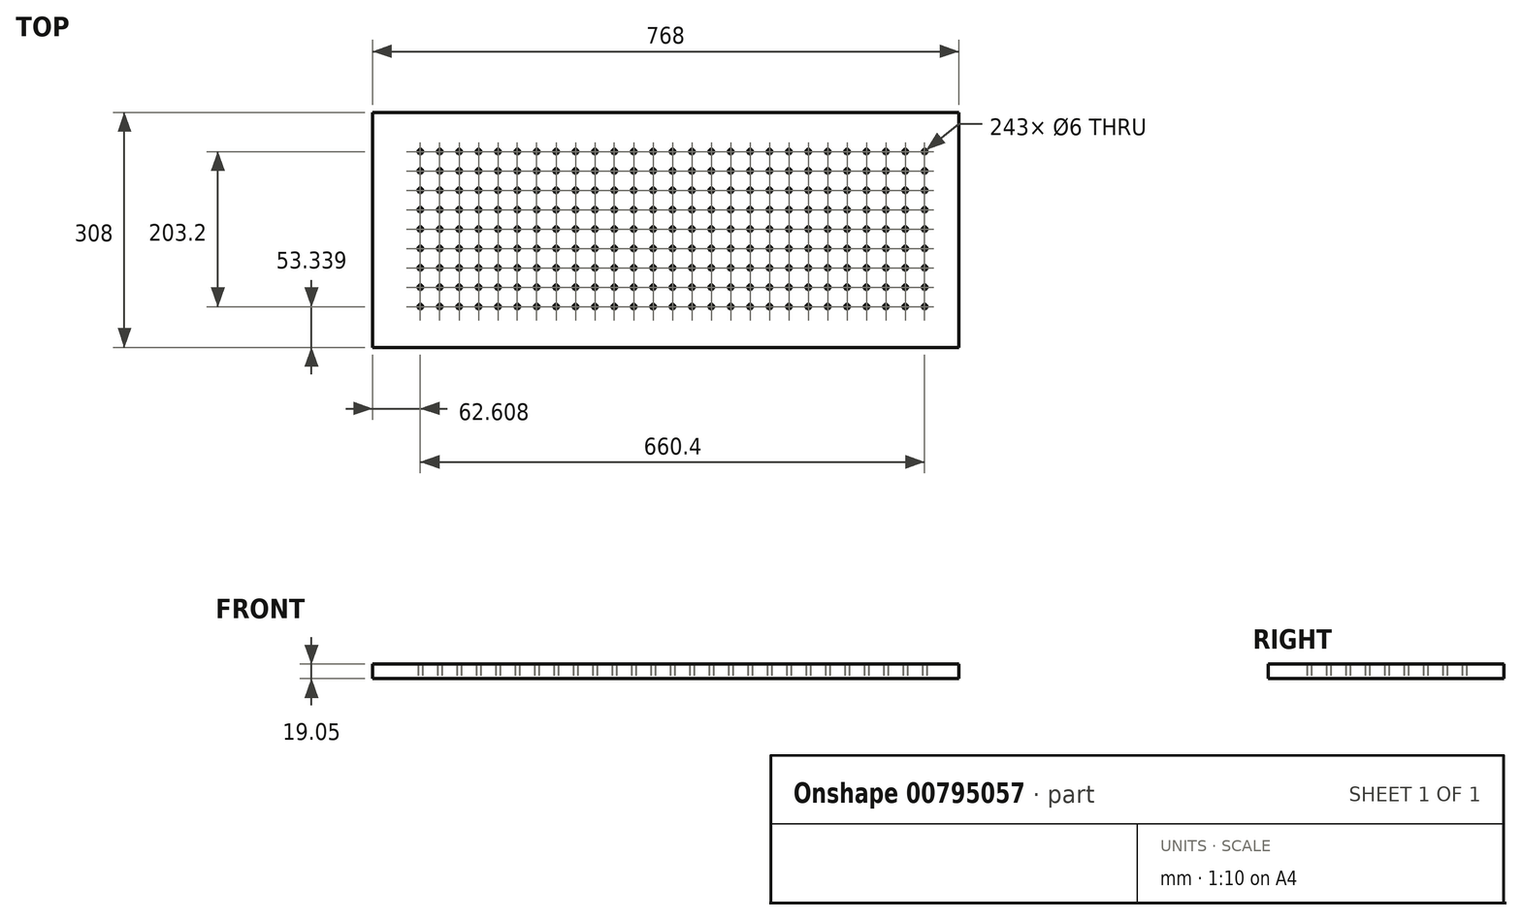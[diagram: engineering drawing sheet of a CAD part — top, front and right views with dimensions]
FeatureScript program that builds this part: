
annotation { "Feature Type Name" : "Feature", "Feature Type Description" : "" }
export const myFeature = defineFeature(function(context is Context, id is Id, definition is map)
    precondition{}
    {
        {
            var Q0;
            Q0=qCreatedBy(makeId("Top.planeOp"),FACE);
            var sketch = newSketch(context, id + "F0", { "sketchPlane" : qUnion([Q0])});
            skLineSegment(sketch, "E0", {"start": v(-588.45, -721.98) * mm, "end": v(179.55, -721.98) * mm});
            skLineSegment(sketch, "E1", {"start": v(179.55, -721.98) * mm, "end": v(179.55, -413.98) * mm});
            skLineSegment(sketch, "E2", {"start": v(179.55, -413.98) * mm, "end": v(-588.45, -413.98) * mm});
            skCircle(sketch, "E3.0.15.2", {"center": v(-475.04, -465.44) * mm, "radius": 3 * mm});
            skCircle(sketch, "E3.0.15.4", {"center": v(-297.24, -465.44) * mm, "radius": 3 * mm});
            skCircle(sketch, "E3.0.15.5", {"center": v(-246.44, -465.44) * mm, "radius": 3 * mm});
            skCircle(sketch, "E3.0.15.6", {"center": v(-373.44, -465.44) * mm, "radius": 3 * mm});
            skCircle(sketch, "E3.0.15.7", {"center": v(-94.04, -465.44) * mm, "radius": 3 * mm});
            skCircle(sketch, "E3.0.15.8", {"center": v(-348.04, -465.44) * mm, "radius": 3 * mm});
            skCircle(sketch, "E3.0.15.9", {"center": v(-144.84, -465.44) * mm, "radius": 3 * mm});
            skCircle(sketch, "E3.0.15.11", {"center": v(-424.24, -465.44) * mm, "radius": 3 * mm});
            skCircle(sketch, "E3.0.15.12", {"center": v(7.56, -465.44) * mm, "radius": 3 * mm});
            skCircle(sketch, "E3.0.15.15", {"center": v(134.56, -465.44) * mm, "radius": 3 * mm});
            skCircle(sketch, "E3.0.15.17", {"center": v(109.16, -465.44) * mm, "radius": 3 * mm});
            skCircle(sketch, "E3.0.15.18", {"center": v(-119.44, -465.44) * mm, "radius": 3 * mm});
            skCircle(sketch, "E3.0.15.20", {"center": v(83.76, -465.44) * mm, "radius": 3 * mm});
            skCircle(sketch, "E3.0.15.21", {"center": v(-500.44, -465.44) * mm, "radius": 3 * mm});
            skCircle(sketch, "E3.0.15.22", {"center": v(58.36, -465.44) * mm, "radius": 3 * mm});
            skCircle(sketch, "E3.0.15.23", {"center": v(-525.84, -465.44) * mm, "radius": 3 * mm});
            skCircle(sketch, "E3.0.15.24", {"center": v(-17.84, -465.44) * mm, "radius": 3 * mm});
            skCircle(sketch, "E3.0.15.25", {"center": v(-398.84, -465.44) * mm, "radius": 3 * mm});
            skCircle(sketch, "E3.0.15.27", {"center": v(-43.24, -465.44) * mm, "radius": 3 * mm});
            skCircle(sketch, "E3.0.15.28", {"center": v(-68.64, -465.44) * mm, "radius": 3 * mm});
            skCircle(sketch, "E3.0.15.29", {"center": v(-322.64, -465.44) * mm, "radius": 3 * mm});
            skCircle(sketch, "E3.0.15.30", {"center": v(-221.04, -465.44) * mm, "radius": 3 * mm});
            skCircle(sketch, "E3.0.15.31", {"center": v(-195.64, -465.44) * mm, "radius": 3 * mm});
            skCircle(sketch, "E3.0.15.32", {"center": v(-170.24, -465.44) * mm, "radius": 3 * mm});
            skCircle(sketch, "E3.0.15.34", {"center": v(-449.64, -465.44) * mm, "radius": 3 * mm});
            skCircle(sketch, "E3.0.15.35", {"center": v(-271.84, -465.44) * mm, "radius": 3 * mm});
            skCircle(sketch, "E3.0.15.36", {"center": v(32.96, -465.44) * mm, "radius": 3 * mm});
            skCircle(sketch, "E3.0.15.37", {"center": v(-500.44, -465.44) * mm, "radius": 3 * mm});
            skCircle(sketch, "E3.0.15.38", {"center": v(-43.24, -465.44) * mm, "radius": 3 * mm});
            skCircle(sketch, "E3.0.15.39", {"center": v(-348.04, -465.44) * mm, "radius": 3 * mm});
            skCircle(sketch, "E3.0.15.40", {"center": v(-68.64, -465.44) * mm, "radius": 3 * mm});
            skCircle(sketch, "E3.0.15.41", {"center": v(-398.84, -465.44) * mm, "radius": 3 * mm});
            skCircle(sketch, "E3.0.15.42", {"center": v(-246.44, -465.44) * mm, "radius": 3 * mm});
            skCircle(sketch, "E3.0.15.44", {"center": v(32.96, -465.44) * mm, "radius": 3 * mm});
            skCircle(sketch, "E3.0.15.45", {"center": v(-195.64, -465.44) * mm, "radius": 3 * mm});
            skCircle(sketch, "E3.0.15.47", {"center": v(-322.64, -465.44) * mm, "radius": 3 * mm});
            skCircle(sketch, "E3.0.15.49", {"center": v(-17.84, -465.44) * mm, "radius": 3 * mm});
            skCircle(sketch, "E3.0.15.50", {"center": v(134.56, -465.44) * mm, "radius": 3 * mm});
            skCircle(sketch, "E3.0.15.51", {"center": v(-449.64, -465.44) * mm, "radius": 3 * mm});
            skCircle(sketch, "E3.0.15.53", {"center": v(-170.24, -465.44) * mm, "radius": 3 * mm});
            skCircle(sketch, "E3.0.15.54", {"center": v(-119.44, -465.44) * mm, "radius": 3 * mm});
            skCircle(sketch, "E3.0.15.55", {"center": v(-373.44, -465.44) * mm, "radius": 3 * mm});
            skCircle(sketch, "E3.0.15.56", {"center": v(109.16, -465.44) * mm, "radius": 3 * mm});
            skCircle(sketch, "E3.0.15.57", {"center": v(-424.24, -465.44) * mm, "radius": 3 * mm});
            skCircle(sketch, "E3.0.15.58", {"center": v(-525.84, -465.44) * mm, "radius": 3 * mm});
            skCircle(sketch, "E3.0.15.59", {"center": v(-94.04, -465.44) * mm, "radius": 3 * mm});
            skCircle(sketch, "E3.0.15.60", {"center": v(-475.04, -465.44) * mm, "radius": 3 * mm});
            skCircle(sketch, "E3.0.15.61", {"center": v(58.36, -465.44) * mm, "radius": 3 * mm});
            skCircle(sketch, "E3.0.15.63", {"center": v(7.56, -465.44) * mm, "radius": 3 * mm});
            skCircle(sketch, "E3.0.15.64", {"center": v(-297.24, -465.44) * mm, "radius": 3 * mm});
            skCircle(sketch, "E3.0.15.67", {"center": v(-144.84, -465.44) * mm, "radius": 3 * mm});
            skCircle(sketch, "E3.0.15.68", {"center": v(-221.04, -465.44) * mm, "radius": 3 * mm});
            skCircle(sketch, "E3.0.15.69", {"center": v(-271.84, -465.44) * mm, "radius": 3 * mm});
            skCircle(sketch, "E3.0.15.70", {"center": v(83.76, -465.44) * mm, "radius": 3 * mm});
            skCircle(sketch, "E3.0.15.71", {"center": v(134.56, -465.44) * mm, "radius": 3 * mm});
            skCircle(sketch, "E3.0.15.72", {"center": v(-424.24, -465.44) * mm, "radius": 3 * mm});
            skCircle(sketch, "E3.0.15.73", {"center": v(-195.64, -465.44) * mm, "radius": 3 * mm});
            skCircle(sketch, "E3.0.15.74", {"center": v(-525.84, -465.44) * mm, "radius": 3 * mm});
            skCircle(sketch, "E3.0.15.75", {"center": v(109.16, -465.44) * mm, "radius": 3 * mm});
            skCircle(sketch, "E3.0.15.76", {"center": v(-246.44, -465.44) * mm, "radius": 3 * mm});
            skCircle(sketch, "E3.0.15.77", {"center": v(-449.64, -465.44) * mm, "radius": 3 * mm});
            skCircle(sketch, "E3.0.15.78", {"center": v(-144.84, -465.44) * mm, "radius": 3 * mm});
            skCircle(sketch, "E3.0.15.79", {"center": v(-348.04, -465.44) * mm, "radius": 3 * mm});
            skCircle(sketch, "E3.0.15.80", {"center": v(-94.04, -465.44) * mm, "radius": 3 * mm});
            skCircle(sketch, "E3.0.15.81", {"center": v(32.96, -465.44) * mm, "radius": 3 * mm});
            skCircle(sketch, "E3.0.15.82", {"center": v(-68.64, -465.44) * mm, "radius": 3 * mm});
            skCircle(sketch, "E3.0.15.84", {"center": v(-373.44, -465.44) * mm, "radius": 3 * mm});
            skCircle(sketch, "E3.0.15.86", {"center": v(-170.24, -465.44) * mm, "radius": 3 * mm});
            skCircle(sketch, "E3.0.15.88", {"center": v(-17.84, -465.44) * mm, "radius": 3 * mm});
            skCircle(sketch, "E3.0.15.89", {"center": v(-221.04, -465.44) * mm, "radius": 3 * mm});
            skCircle(sketch, "E3.0.15.90", {"center": v(-119.44, -465.44) * mm, "radius": 3 * mm});
            skCircle(sketch, "E3.0.15.92", {"center": v(-475.04, -465.44) * mm, "radius": 3 * mm});
            skCircle(sketch, "E3.0.15.93", {"center": v(-297.24, -465.44) * mm, "radius": 3 * mm});
            skCircle(sketch, "E3.0.15.94", {"center": v(-43.24, -465.44) * mm, "radius": 3 * mm});
            skCircle(sketch, "E3.0.15.95", {"center": v(83.76, -465.44) * mm, "radius": 3 * mm});
            skCircle(sketch, "E3.0.15.97", {"center": v(-500.44, -465.44) * mm, "radius": 3 * mm});
            skCircle(sketch, "E3.0.15.98", {"center": v(-322.64, -465.44) * mm, "radius": 3 * mm});
            skCircle(sketch, "E3.0.15.100", {"center": v(-398.84, -465.44) * mm, "radius": 3 * mm});
            skCircle(sketch, "E3.0.15.102", {"center": v(58.36, -465.44) * mm, "radius": 3 * mm});
            skCircle(sketch, "E3.0.15.103", {"center": v(7.56, -465.44) * mm, "radius": 3 * mm});
            skCircle(sketch, "E3.0.15.104", {"center": v(-271.84, -465.44) * mm, "radius": 3 * mm});
            skCircle(sketch, "E3.0.16.2", {"center": v(-475.04, -490.84) * mm, "radius": 3 * mm});
            skCircle(sketch, "E3.0.16.4", {"center": v(-297.24, -490.84) * mm, "radius": 3 * mm});
            skCircle(sketch, "E3.0.16.5", {"center": v(-246.44, -490.84) * mm, "radius": 3 * mm});
            skCircle(sketch, "E3.0.16.6", {"center": v(-373.44, -490.84) * mm, "radius": 3 * mm});
            skCircle(sketch, "E3.0.16.7", {"center": v(-94.04, -490.84) * mm, "radius": 3 * mm});
            skCircle(sketch, "E3.0.16.8", {"center": v(-348.04, -490.84) * mm, "radius": 3 * mm});
            skCircle(sketch, "E3.0.16.9", {"center": v(-144.84, -490.84) * mm, "radius": 3 * mm});
            skCircle(sketch, "E3.0.16.11", {"center": v(-424.24, -490.84) * mm, "radius": 3 * mm});
            skCircle(sketch, "E3.0.16.12", {"center": v(7.56, -490.84) * mm, "radius": 3 * mm});
            skCircle(sketch, "E3.0.16.15", {"center": v(134.56, -490.84) * mm, "radius": 3 * mm});
            skCircle(sketch, "E3.0.16.17", {"center": v(109.16, -490.84) * mm, "radius": 3 * mm});
            skCircle(sketch, "E3.0.16.18", {"center": v(-119.44, -490.84) * mm, "radius": 3 * mm});
            skCircle(sketch, "E3.0.16.20", {"center": v(83.76, -490.84) * mm, "radius": 3 * mm});
            skCircle(sketch, "E3.0.16.21", {"center": v(-500.44, -490.84) * mm, "radius": 3 * mm});
            skCircle(sketch, "E3.0.16.22", {"center": v(58.36, -490.84) * mm, "radius": 3 * mm});
            skCircle(sketch, "E3.0.16.23", {"center": v(-525.84, -490.84) * mm, "radius": 3 * mm});
            skCircle(sketch, "E3.0.16.24", {"center": v(-17.84, -490.84) * mm, "radius": 3 * mm});
            skCircle(sketch, "E3.0.16.25", {"center": v(-398.84, -490.84) * mm, "radius": 3 * mm});
            skCircle(sketch, "E3.0.16.27", {"center": v(-43.24, -490.84) * mm, "radius": 3 * mm});
            skCircle(sketch, "E3.0.16.28", {"center": v(-68.64, -490.84) * mm, "radius": 3 * mm});
            skCircle(sketch, "E3.0.16.29", {"center": v(-322.64, -490.84) * mm, "radius": 3 * mm});
            skCircle(sketch, "E3.0.16.30", {"center": v(-221.04, -490.84) * mm, "radius": 3 * mm});
            skCircle(sketch, "E3.0.16.31", {"center": v(-195.64, -490.84) * mm, "radius": 3 * mm});
            skCircle(sketch, "E3.0.16.32", {"center": v(-170.24, -490.84) * mm, "radius": 3 * mm});
            skCircle(sketch, "E3.0.16.34", {"center": v(-449.64, -490.84) * mm, "radius": 3 * mm});
            skCircle(sketch, "E3.0.16.35", {"center": v(-271.84, -490.84) * mm, "radius": 3 * mm});
            skCircle(sketch, "E3.0.16.36", {"center": v(32.96, -490.84) * mm, "radius": 3 * mm});
            skCircle(sketch, "E3.0.16.37", {"center": v(-500.44, -490.84) * mm, "radius": 3 * mm});
            skCircle(sketch, "E3.0.16.38", {"center": v(-43.24, -490.84) * mm, "radius": 3 * mm});
            skCircle(sketch, "E3.0.16.39", {"center": v(-348.04, -490.84) * mm, "radius": 3 * mm});
            skCircle(sketch, "E3.0.16.40", {"center": v(-68.64, -490.84) * mm, "radius": 3 * mm});
            skCircle(sketch, "E3.0.16.41", {"center": v(-398.84, -490.84) * mm, "radius": 3 * mm});
            skCircle(sketch, "E3.0.16.42", {"center": v(-246.44, -490.84) * mm, "radius": 3 * mm});
            skCircle(sketch, "E3.0.16.44", {"center": v(32.96, -490.84) * mm, "radius": 3 * mm});
            skCircle(sketch, "E3.0.16.45", {"center": v(-195.64, -490.84) * mm, "radius": 3 * mm});
            skCircle(sketch, "E3.0.16.47", {"center": v(-322.64, -490.84) * mm, "radius": 3 * mm});
            skCircle(sketch, "E3.0.16.49", {"center": v(-17.84, -490.84) * mm, "radius": 3 * mm});
            skCircle(sketch, "E3.0.16.50", {"center": v(134.56, -490.84) * mm, "radius": 3 * mm});
            skCircle(sketch, "E3.0.16.51", {"center": v(-449.64, -490.84) * mm, "radius": 3 * mm});
            skCircle(sketch, "E3.0.16.53", {"center": v(-170.24, -490.84) * mm, "radius": 3 * mm});
            skCircle(sketch, "E3.0.16.54", {"center": v(-119.44, -490.84) * mm, "radius": 3 * mm});
            skCircle(sketch, "E3.0.16.55", {"center": v(-373.44, -490.84) * mm, "radius": 3 * mm});
            skCircle(sketch, "E3.0.16.56", {"center": v(109.16, -490.84) * mm, "radius": 3 * mm});
            skCircle(sketch, "E3.0.16.57", {"center": v(-424.24, -490.84) * mm, "radius": 3 * mm});
            skCircle(sketch, "E3.0.16.58", {"center": v(-525.84, -490.84) * mm, "radius": 3 * mm});
            skCircle(sketch, "E3.0.16.59", {"center": v(-94.04, -490.84) * mm, "radius": 3 * mm});
            skCircle(sketch, "E3.0.16.60", {"center": v(-475.04, -490.84) * mm, "radius": 3 * mm});
            skCircle(sketch, "E3.0.16.61", {"center": v(58.36, -490.84) * mm, "radius": 3 * mm});
            skCircle(sketch, "E3.0.16.63", {"center": v(7.56, -490.84) * mm, "radius": 3 * mm});
            skCircle(sketch, "E3.0.16.64", {"center": v(-297.24, -490.84) * mm, "radius": 3 * mm});
            skCircle(sketch, "E3.0.16.67", {"center": v(-144.84, -490.84) * mm, "radius": 3 * mm});
            skCircle(sketch, "E3.0.16.68", {"center": v(-221.04, -490.84) * mm, "radius": 3 * mm});
            skCircle(sketch, "E3.0.16.69", {"center": v(-271.84, -490.84) * mm, "radius": 3 * mm});
            skCircle(sketch, "E3.0.16.70", {"center": v(83.76, -490.84) * mm, "radius": 3 * mm});
            skCircle(sketch, "E3.0.16.71", {"center": v(134.56, -490.84) * mm, "radius": 3 * mm});
            skCircle(sketch, "E3.0.16.72", {"center": v(-424.24, -490.84) * mm, "radius": 3 * mm});
            skCircle(sketch, "E3.0.16.73", {"center": v(-195.64, -490.84) * mm, "radius": 3 * mm});
            skCircle(sketch, "E3.0.16.74", {"center": v(-525.84, -490.84) * mm, "radius": 3 * mm});
            skCircle(sketch, "E3.0.16.75", {"center": v(109.16, -490.84) * mm, "radius": 3 * mm});
            skCircle(sketch, "E3.0.16.76", {"center": v(-246.44, -490.84) * mm, "radius": 3 * mm});
            skCircle(sketch, "E3.0.16.77", {"center": v(-449.64, -490.84) * mm, "radius": 3 * mm});
            skCircle(sketch, "E3.0.16.78", {"center": v(-144.84, -490.84) * mm, "radius": 3 * mm});
            skCircle(sketch, "E3.0.16.79", {"center": v(-348.04, -490.84) * mm, "radius": 3 * mm});
            skCircle(sketch, "E3.0.16.80", {"center": v(-94.04, -490.84) * mm, "radius": 3 * mm});
            skCircle(sketch, "E3.0.16.81", {"center": v(32.96, -490.84) * mm, "radius": 3 * mm});
            skCircle(sketch, "E3.0.16.82", {"center": v(-68.64, -490.84) * mm, "radius": 3 * mm});
            skCircle(sketch, "E3.0.16.84", {"center": v(-373.44, -490.84) * mm, "radius": 3 * mm});
            skCircle(sketch, "E3.0.16.86", {"center": v(-170.24, -490.84) * mm, "radius": 3 * mm});
            skCircle(sketch, "E3.0.16.88", {"center": v(-17.84, -490.84) * mm, "radius": 3 * mm});
            skCircle(sketch, "E3.0.16.89", {"center": v(-221.04, -490.84) * mm, "radius": 3 * mm});
            skCircle(sketch, "E3.0.16.90", {"center": v(-119.44, -490.84) * mm, "radius": 3 * mm});
            skCircle(sketch, "E3.0.16.92", {"center": v(-475.04, -490.84) * mm, "radius": 3 * mm});
            skCircle(sketch, "E3.0.16.93", {"center": v(-297.24, -490.84) * mm, "radius": 3 * mm});
            skCircle(sketch, "E3.0.16.94", {"center": v(-43.24, -490.84) * mm, "radius": 3 * mm});
            skCircle(sketch, "E3.0.16.95", {"center": v(83.76, -490.84) * mm, "radius": 3 * mm});
            skCircle(sketch, "E3.0.16.97", {"center": v(-500.44, -490.84) * mm, "radius": 3 * mm});
            skCircle(sketch, "E3.0.16.98", {"center": v(-322.64, -490.84) * mm, "radius": 3 * mm});
            skCircle(sketch, "E3.0.16.100", {"center": v(-398.84, -490.84) * mm, "radius": 3 * mm});
            skCircle(sketch, "E3.0.16.102", {"center": v(58.36, -490.84) * mm, "radius": 3 * mm});
            skCircle(sketch, "E3.0.16.103", {"center": v(7.56, -490.84) * mm, "radius": 3 * mm});
            skCircle(sketch, "E3.0.16.104", {"center": v(-271.84, -490.84) * mm, "radius": 3 * mm});
            skCircle(sketch, "E3.0.17.2", {"center": v(-475.04, -516.24) * mm, "radius": 3 * mm});
            skCircle(sketch, "E3.0.17.4", {"center": v(-297.24, -516.24) * mm, "radius": 3 * mm});
            skCircle(sketch, "E3.0.17.5", {"center": v(-246.44, -516.24) * mm, "radius": 3 * mm});
            skCircle(sketch, "E3.0.17.6", {"center": v(-373.44, -516.24) * mm, "radius": 3 * mm});
            skCircle(sketch, "E3.0.17.7", {"center": v(-94.04, -516.24) * mm, "radius": 3 * mm});
            skCircle(sketch, "E3.0.17.8", {"center": v(-348.04, -516.24) * mm, "radius": 3 * mm});
            skCircle(sketch, "E3.0.17.9", {"center": v(-144.84, -516.24) * mm, "radius": 3 * mm});
            skCircle(sketch, "E3.0.17.11", {"center": v(-424.24, -516.24) * mm, "radius": 3 * mm});
            skCircle(sketch, "E3.0.17.12", {"center": v(7.56, -516.24) * mm, "radius": 3 * mm});
            skCircle(sketch, "E3.0.17.15", {"center": v(134.56, -516.24) * mm, "radius": 3 * mm});
            skCircle(sketch, "E3.0.17.17", {"center": v(109.16, -516.24) * mm, "radius": 3 * mm});
            skCircle(sketch, "E3.0.17.18", {"center": v(-119.44, -516.24) * mm, "radius": 3 * mm});
            skCircle(sketch, "E3.0.17.20", {"center": v(83.76, -516.24) * mm, "radius": 3 * mm});
            skCircle(sketch, "E3.0.17.21", {"center": v(-500.44, -516.24) * mm, "radius": 3 * mm});
            skCircle(sketch, "E3.0.17.22", {"center": v(58.36, -516.24) * mm, "radius": 3 * mm});
            skCircle(sketch, "E3.0.17.23", {"center": v(-525.84, -516.24) * mm, "radius": 3 * mm});
            skCircle(sketch, "E3.0.17.24", {"center": v(-17.84, -516.24) * mm, "radius": 3 * mm});
            skCircle(sketch, "E3.0.17.25", {"center": v(-398.84, -516.24) * mm, "radius": 3 * mm});
            skCircle(sketch, "E3.0.17.27", {"center": v(-43.24, -516.24) * mm, "radius": 3 * mm});
            skCircle(sketch, "E3.0.17.28", {"center": v(-68.64, -516.24) * mm, "radius": 3 * mm});
            skCircle(sketch, "E3.0.17.29", {"center": v(-322.64, -516.24) * mm, "radius": 3 * mm});
            skCircle(sketch, "E3.0.17.30", {"center": v(-221.04, -516.24) * mm, "radius": 3 * mm});
            skCircle(sketch, "E3.0.17.31", {"center": v(-195.64, -516.24) * mm, "radius": 3 * mm});
            skCircle(sketch, "E3.0.17.32", {"center": v(-170.24, -516.24) * mm, "radius": 3 * mm});
            skCircle(sketch, "E3.0.17.34", {"center": v(-449.64, -516.24) * mm, "radius": 3 * mm});
            skCircle(sketch, "E3.0.17.35", {"center": v(-271.84, -516.24) * mm, "radius": 3 * mm});
            skCircle(sketch, "E3.0.17.36", {"center": v(32.96, -516.24) * mm, "radius": 3 * mm});
            skCircle(sketch, "E3.0.17.37", {"center": v(-500.44, -516.24) * mm, "radius": 3 * mm});
            skCircle(sketch, "E3.0.17.38", {"center": v(-43.24, -516.24) * mm, "radius": 3 * mm});
            skCircle(sketch, "E3.0.17.39", {"center": v(-348.04, -516.24) * mm, "radius": 3 * mm});
            skCircle(sketch, "E3.0.17.40", {"center": v(-68.64, -516.24) * mm, "radius": 3 * mm});
            skCircle(sketch, "E3.0.17.41", {"center": v(-398.84, -516.24) * mm, "radius": 3 * mm});
            skCircle(sketch, "E3.0.17.42", {"center": v(-246.44, -516.24) * mm, "radius": 3 * mm});
            skCircle(sketch, "E3.0.17.44", {"center": v(32.96, -516.24) * mm, "radius": 3 * mm});
            skCircle(sketch, "E3.0.17.45", {"center": v(-195.64, -516.24) * mm, "radius": 3 * mm});
            skCircle(sketch, "E3.0.17.47", {"center": v(-322.64, -516.24) * mm, "radius": 3 * mm});
            skCircle(sketch, "E3.0.17.49", {"center": v(-17.84, -516.24) * mm, "radius": 3 * mm});
            skCircle(sketch, "E3.0.17.50", {"center": v(134.56, -516.24) * mm, "radius": 3 * mm});
            skCircle(sketch, "E3.0.17.51", {"center": v(-449.64, -516.24) * mm, "radius": 3 * mm});
            skCircle(sketch, "E3.0.17.53", {"center": v(-170.24, -516.24) * mm, "radius": 3 * mm});
            skCircle(sketch, "E3.0.17.54", {"center": v(-119.44, -516.24) * mm, "radius": 3 * mm});
            skCircle(sketch, "E3.0.17.55", {"center": v(-373.44, -516.24) * mm, "radius": 3 * mm});
            skCircle(sketch, "E3.0.17.56", {"center": v(109.16, -516.24) * mm, "radius": 3 * mm});
            skCircle(sketch, "E3.0.17.57", {"center": v(-424.24, -516.24) * mm, "radius": 3 * mm});
            skCircle(sketch, "E3.0.17.58", {"center": v(-525.84, -516.24) * mm, "radius": 3 * mm});
            skCircle(sketch, "E3.0.17.59", {"center": v(-94.04, -516.24) * mm, "radius": 3 * mm});
            skCircle(sketch, "E3.0.17.60", {"center": v(-475.04, -516.24) * mm, "radius": 3 * mm});
            skCircle(sketch, "E3.0.17.61", {"center": v(58.36, -516.24) * mm, "radius": 3 * mm});
            skCircle(sketch, "E3.0.17.63", {"center": v(7.56, -516.24) * mm, "radius": 3 * mm});
            skCircle(sketch, "E3.0.17.64", {"center": v(-297.24, -516.24) * mm, "radius": 3 * mm});
            skCircle(sketch, "E3.0.17.67", {"center": v(-144.84, -516.24) * mm, "radius": 3 * mm});
            skCircle(sketch, "E3.0.17.68", {"center": v(-221.04, -516.24) * mm, "radius": 3 * mm});
            skCircle(sketch, "E3.0.17.69", {"center": v(-271.84, -516.24) * mm, "radius": 3 * mm});
            skCircle(sketch, "E3.0.17.70", {"center": v(83.76, -516.24) * mm, "radius": 3 * mm});
            skCircle(sketch, "E3.0.17.71", {"center": v(134.56, -516.24) * mm, "radius": 3 * mm});
            skCircle(sketch, "E3.0.17.72", {"center": v(-424.24, -516.24) * mm, "radius": 3 * mm});
            skCircle(sketch, "E3.0.17.73", {"center": v(-195.64, -516.24) * mm, "radius": 3 * mm});
            skCircle(sketch, "E3.0.17.74", {"center": v(-525.84, -516.24) * mm, "radius": 3 * mm});
            skCircle(sketch, "E3.0.17.75", {"center": v(109.16, -516.24) * mm, "radius": 3 * mm});
            skCircle(sketch, "E3.0.17.76", {"center": v(-246.44, -516.24) * mm, "radius": 3 * mm});
            skCircle(sketch, "E3.0.17.77", {"center": v(-449.64, -516.24) * mm, "radius": 3 * mm});
            skCircle(sketch, "E3.0.17.78", {"center": v(-144.84, -516.24) * mm, "radius": 3 * mm});
            skCircle(sketch, "E3.0.17.79", {"center": v(-348.04, -516.24) * mm, "radius": 3 * mm});
            skCircle(sketch, "E3.0.17.80", {"center": v(-94.04, -516.24) * mm, "radius": 3 * mm});
            skCircle(sketch, "E3.0.17.81", {"center": v(32.96, -516.24) * mm, "radius": 3 * mm});
            skCircle(sketch, "E3.0.17.82", {"center": v(-68.64, -516.24) * mm, "radius": 3 * mm});
            skCircle(sketch, "E3.0.17.84", {"center": v(-373.44, -516.24) * mm, "radius": 3 * mm});
            skCircle(sketch, "E3.0.17.86", {"center": v(-170.24, -516.24) * mm, "radius": 3 * mm});
            skCircle(sketch, "E3.0.17.88", {"center": v(-17.84, -516.24) * mm, "radius": 3 * mm});
            skCircle(sketch, "E3.0.17.89", {"center": v(-221.04, -516.24) * mm, "radius": 3 * mm});
            skCircle(sketch, "E3.0.17.90", {"center": v(-119.44, -516.24) * mm, "radius": 3 * mm});
            skCircle(sketch, "E3.0.17.92", {"center": v(-475.04, -516.24) * mm, "radius": 3 * mm});
            skCircle(sketch, "E3.0.17.93", {"center": v(-297.24, -516.24) * mm, "radius": 3 * mm});
            skCircle(sketch, "E3.0.17.94", {"center": v(-43.24, -516.24) * mm, "radius": 3 * mm});
            skCircle(sketch, "E3.0.17.95", {"center": v(83.76, -516.24) * mm, "radius": 3 * mm});
            skCircle(sketch, "E3.0.17.97", {"center": v(-500.44, -516.24) * mm, "radius": 3 * mm});
            skCircle(sketch, "E3.0.17.98", {"center": v(-322.64, -516.24) * mm, "radius": 3 * mm});
            skCircle(sketch, "E3.0.17.100", {"center": v(-398.84, -516.24) * mm, "radius": 3 * mm});
            skCircle(sketch, "E3.0.17.102", {"center": v(58.36, -516.24) * mm, "radius": 3 * mm});
            skCircle(sketch, "E3.0.17.103", {"center": v(7.56, -516.24) * mm, "radius": 3 * mm});
            skCircle(sketch, "E3.0.17.104", {"center": v(-271.84, -516.24) * mm, "radius": 3 * mm});
            skCircle(sketch, "E3.0.18.2", {"center": v(-475.04, -541.64) * mm, "radius": 3 * mm});
            skCircle(sketch, "E3.0.18.4", {"center": v(-297.24, -541.64) * mm, "radius": 3 * mm});
            skCircle(sketch, "E3.0.18.5", {"center": v(-246.44, -541.64) * mm, "radius": 3 * mm});
            skCircle(sketch, "E3.0.18.6", {"center": v(-373.44, -541.64) * mm, "radius": 3 * mm});
            skCircle(sketch, "E3.0.18.7", {"center": v(-94.04, -541.64) * mm, "radius": 3 * mm});
            skCircle(sketch, "E3.0.18.8", {"center": v(-348.04, -541.64) * mm, "radius": 3 * mm});
            skCircle(sketch, "E3.0.18.9", {"center": v(-144.84, -541.64) * mm, "radius": 3 * mm});
            skCircle(sketch, "E3.0.18.11", {"center": v(-424.24, -541.64) * mm, "radius": 3 * mm});
            skCircle(sketch, "E3.0.18.12", {"center": v(7.56, -541.64) * mm, "radius": 3 * mm});
            skCircle(sketch, "E3.0.18.15", {"center": v(134.56, -541.64) * mm, "radius": 3 * mm});
            skCircle(sketch, "E3.0.18.17", {"center": v(109.16, -541.64) * mm, "radius": 3 * mm});
            skCircle(sketch, "E3.0.18.18", {"center": v(-119.44, -541.64) * mm, "radius": 3 * mm});
            skCircle(sketch, "E3.0.18.20", {"center": v(83.76, -541.64) * mm, "radius": 3 * mm});
            skCircle(sketch, "E3.0.18.21", {"center": v(-500.44, -541.64) * mm, "radius": 3 * mm});
            skCircle(sketch, "E3.0.18.22", {"center": v(58.36, -541.64) * mm, "radius": 3 * mm});
            skCircle(sketch, "E3.0.18.23", {"center": v(-525.84, -541.64) * mm, "radius": 3 * mm});
            skCircle(sketch, "E3.0.18.24", {"center": v(-17.84, -541.64) * mm, "radius": 3 * mm});
            skCircle(sketch, "E3.0.18.25", {"center": v(-398.84, -541.64) * mm, "radius": 3 * mm});
            skCircle(sketch, "E3.0.18.27", {"center": v(-43.24, -541.64) * mm, "radius": 3 * mm});
            skCircle(sketch, "E3.0.18.28", {"center": v(-68.64, -541.64) * mm, "radius": 3 * mm});
            skCircle(sketch, "E3.0.18.29", {"center": v(-322.64, -541.64) * mm, "radius": 3 * mm});
            skCircle(sketch, "E3.0.18.30", {"center": v(-221.04, -541.64) * mm, "radius": 3 * mm});
            skCircle(sketch, "E3.0.18.31", {"center": v(-195.64, -541.64) * mm, "radius": 3 * mm});
            skCircle(sketch, "E3.0.18.32", {"center": v(-170.24, -541.64) * mm, "radius": 3 * mm});
            skCircle(sketch, "E3.0.18.34", {"center": v(-449.64, -541.64) * mm, "radius": 3 * mm});
            skCircle(sketch, "E3.0.18.35", {"center": v(-271.84, -541.64) * mm, "radius": 3 * mm});
            skCircle(sketch, "E3.0.18.36", {"center": v(32.96, -541.64) * mm, "radius": 3 * mm});
            skCircle(sketch, "E3.0.18.37", {"center": v(-500.44, -541.64) * mm, "radius": 3 * mm});
            skCircle(sketch, "E3.0.18.38", {"center": v(-43.24, -541.64) * mm, "radius": 3 * mm});
            skCircle(sketch, "E3.0.18.39", {"center": v(-348.04, -541.64) * mm, "radius": 3 * mm});
            skCircle(sketch, "E3.0.18.40", {"center": v(-68.64, -541.64) * mm, "radius": 3 * mm});
            skCircle(sketch, "E3.0.18.41", {"center": v(-398.84, -541.64) * mm, "radius": 3 * mm});
            skCircle(sketch, "E3.0.18.42", {"center": v(-246.44, -541.64) * mm, "radius": 3 * mm});
            skCircle(sketch, "E3.0.18.44", {"center": v(32.96, -541.64) * mm, "radius": 3 * mm});
            skCircle(sketch, "E3.0.18.45", {"center": v(-195.64, -541.64) * mm, "radius": 3 * mm});
            skCircle(sketch, "E3.0.18.47", {"center": v(-322.64, -541.64) * mm, "radius": 3 * mm});
            skCircle(sketch, "E3.0.18.49", {"center": v(-17.84, -541.64) * mm, "radius": 3 * mm});
            skCircle(sketch, "E3.0.18.50", {"center": v(134.56, -541.64) * mm, "radius": 3 * mm});
            skCircle(sketch, "E3.0.18.51", {"center": v(-449.64, -541.64) * mm, "radius": 3 * mm});
            skCircle(sketch, "E3.0.18.53", {"center": v(-170.24, -541.64) * mm, "radius": 3 * mm});
            skCircle(sketch, "E3.0.18.54", {"center": v(-119.44, -541.64) * mm, "radius": 3 * mm});
            skCircle(sketch, "E3.0.18.55", {"center": v(-373.44, -541.64) * mm, "radius": 3 * mm});
            skCircle(sketch, "E3.0.18.56", {"center": v(109.16, -541.64) * mm, "radius": 3 * mm});
            skCircle(sketch, "E3.0.18.57", {"center": v(-424.24, -541.64) * mm, "radius": 3 * mm});
            skCircle(sketch, "E3.0.18.58", {"center": v(-525.84, -541.64) * mm, "radius": 3 * mm});
            skCircle(sketch, "E3.0.18.59", {"center": v(-94.04, -541.64) * mm, "radius": 3 * mm});
            skCircle(sketch, "E3.0.18.60", {"center": v(-475.04, -541.64) * mm, "radius": 3 * mm});
            skCircle(sketch, "E3.0.18.61", {"center": v(58.36, -541.64) * mm, "radius": 3 * mm});
            skCircle(sketch, "E3.0.18.63", {"center": v(7.56, -541.64) * mm, "radius": 3 * mm});
            skCircle(sketch, "E3.0.18.64", {"center": v(-297.24, -541.64) * mm, "radius": 3 * mm});
            skCircle(sketch, "E3.0.18.67", {"center": v(-144.84, -541.64) * mm, "radius": 3 * mm});
            skCircle(sketch, "E3.0.18.68", {"center": v(-221.04, -541.64) * mm, "radius": 3 * mm});
            skCircle(sketch, "E3.0.18.69", {"center": v(-271.84, -541.64) * mm, "radius": 3 * mm});
            skCircle(sketch, "E3.0.18.70", {"center": v(83.76, -541.64) * mm, "radius": 3 * mm});
            skCircle(sketch, "E3.0.18.71", {"center": v(134.56, -541.64) * mm, "radius": 3 * mm});
            skCircle(sketch, "E3.0.18.72", {"center": v(-424.24, -541.64) * mm, "radius": 3 * mm});
            skCircle(sketch, "E3.0.18.73", {"center": v(-195.64, -541.64) * mm, "radius": 3 * mm});
            skCircle(sketch, "E3.0.18.74", {"center": v(-525.84, -541.64) * mm, "radius": 3 * mm});
            skCircle(sketch, "E3.0.18.75", {"center": v(109.16, -541.64) * mm, "radius": 3 * mm});
            skCircle(sketch, "E3.0.18.76", {"center": v(-246.44, -541.64) * mm, "radius": 3 * mm});
            skCircle(sketch, "E3.0.18.77", {"center": v(-449.64, -541.64) * mm, "radius": 3 * mm});
            skCircle(sketch, "E3.0.18.78", {"center": v(-144.84, -541.64) * mm, "radius": 3 * mm});
            skCircle(sketch, "E3.0.18.79", {"center": v(-348.04, -541.64) * mm, "radius": 3 * mm});
            skCircle(sketch, "E3.0.18.80", {"center": v(-94.04, -541.64) * mm, "radius": 3 * mm});
            skCircle(sketch, "E3.0.18.81", {"center": v(32.96, -541.64) * mm, "radius": 3 * mm});
            skCircle(sketch, "E3.0.18.82", {"center": v(-68.64, -541.64) * mm, "radius": 3 * mm});
            skCircle(sketch, "E3.0.18.84", {"center": v(-373.44, -541.64) * mm, "radius": 3 * mm});
            skCircle(sketch, "E3.0.18.86", {"center": v(-170.24, -541.64) * mm, "radius": 3 * mm});
            skCircle(sketch, "E3.0.18.88", {"center": v(-17.84, -541.64) * mm, "radius": 3 * mm});
            skCircle(sketch, "E3.0.18.89", {"center": v(-221.04, -541.64) * mm, "radius": 3 * mm});
            skCircle(sketch, "E3.0.18.90", {"center": v(-119.44, -541.64) * mm, "radius": 3 * mm});
            skCircle(sketch, "E3.0.18.92", {"center": v(-475.04, -541.64) * mm, "radius": 3 * mm});
            skCircle(sketch, "E3.0.18.93", {"center": v(-297.24, -541.64) * mm, "radius": 3 * mm});
            skCircle(sketch, "E3.0.18.94", {"center": v(-43.24, -541.64) * mm, "radius": 3 * mm});
            skCircle(sketch, "E3.0.18.95", {"center": v(83.76, -541.64) * mm, "radius": 3 * mm});
            skCircle(sketch, "E3.0.18.97", {"center": v(-500.44, -541.64) * mm, "radius": 3 * mm});
            skCircle(sketch, "E3.0.18.98", {"center": v(-322.64, -541.64) * mm, "radius": 3 * mm});
            skCircle(sketch, "E3.0.18.100", {"center": v(-398.84, -541.64) * mm, "radius": 3 * mm});
            skCircle(sketch, "E3.0.18.102", {"center": v(58.36, -541.64) * mm, "radius": 3 * mm});
            skCircle(sketch, "E3.0.18.103", {"center": v(7.56, -541.64) * mm, "radius": 3 * mm});
            skCircle(sketch, "E3.0.18.104", {"center": v(-271.84, -541.64) * mm, "radius": 3 * mm});
            skCircle(sketch, "E3.0.19.2", {"center": v(-475.04, -567.04) * mm, "radius": 3 * mm});
            skCircle(sketch, "E3.0.19.4", {"center": v(-297.24, -567.04) * mm, "radius": 3 * mm});
            skCircle(sketch, "E3.0.19.5", {"center": v(-246.44, -567.04) * mm, "radius": 3 * mm});
            skCircle(sketch, "E3.0.19.6", {"center": v(-373.44, -567.04) * mm, "radius": 3 * mm});
            skCircle(sketch, "E3.0.19.7", {"center": v(-94.04, -567.04) * mm, "radius": 3 * mm});
            skCircle(sketch, "E3.0.19.8", {"center": v(-348.04, -567.04) * mm, "radius": 3 * mm});
            skCircle(sketch, "E3.0.19.9", {"center": v(-144.84, -567.04) * mm, "radius": 3 * mm});
            skCircle(sketch, "E3.0.19.11", {"center": v(-424.24, -567.04) * mm, "radius": 3 * mm});
            skCircle(sketch, "E3.0.19.12", {"center": v(7.56, -567.04) * mm, "radius": 3 * mm});
            skCircle(sketch, "E3.0.19.15", {"center": v(134.56, -567.04) * mm, "radius": 3 * mm});
            skCircle(sketch, "E3.0.19.17", {"center": v(109.16, -567.04) * mm, "radius": 3 * mm});
            skCircle(sketch, "E3.0.19.18", {"center": v(-119.44, -567.04) * mm, "radius": 3 * mm});
            skCircle(sketch, "E3.0.19.20", {"center": v(83.76, -567.04) * mm, "radius": 3 * mm});
            skCircle(sketch, "E3.0.19.21", {"center": v(-500.44, -567.04) * mm, "radius": 3 * mm});
            skCircle(sketch, "E3.0.19.22", {"center": v(58.36, -567.04) * mm, "radius": 3 * mm});
            skCircle(sketch, "E3.0.19.23", {"center": v(-525.84, -567.04) * mm, "radius": 3 * mm});
            skCircle(sketch, "E3.0.19.24", {"center": v(-17.84, -567.04) * mm, "radius": 3 * mm});
            skCircle(sketch, "E3.0.19.25", {"center": v(-398.84, -567.04) * mm, "radius": 3 * mm});
            skCircle(sketch, "E3.0.19.27", {"center": v(-43.24, -567.04) * mm, "radius": 3 * mm});
            skCircle(sketch, "E3.0.19.28", {"center": v(-68.64, -567.04) * mm, "radius": 3 * mm});
            skCircle(sketch, "E3.0.19.29", {"center": v(-322.64, -567.04) * mm, "radius": 3 * mm});
            skCircle(sketch, "E3.0.19.30", {"center": v(-221.04, -567.04) * mm, "radius": 3 * mm});
            skCircle(sketch, "E3.0.19.31", {"center": v(-195.64, -567.04) * mm, "radius": 3 * mm});
            skCircle(sketch, "E3.0.19.32", {"center": v(-170.24, -567.04) * mm, "radius": 3 * mm});
            skCircle(sketch, "E3.0.19.34", {"center": v(-449.64, -567.04) * mm, "radius": 3 * mm});
            skCircle(sketch, "E3.0.19.35", {"center": v(-271.84, -567.04) * mm, "radius": 3 * mm});
            skCircle(sketch, "E3.0.19.36", {"center": v(32.96, -567.04) * mm, "radius": 3 * mm});
            skCircle(sketch, "E3.0.19.37", {"center": v(-500.44, -567.04) * mm, "radius": 3 * mm});
            skCircle(sketch, "E3.0.19.38", {"center": v(-43.24, -567.04) * mm, "radius": 3 * mm});
            skCircle(sketch, "E3.0.19.39", {"center": v(-348.04, -567.04) * mm, "radius": 3 * mm});
            skCircle(sketch, "E3.0.19.40", {"center": v(-68.64, -567.04) * mm, "radius": 3 * mm});
            skCircle(sketch, "E3.0.19.41", {"center": v(-398.84, -567.04) * mm, "radius": 3 * mm});
            skCircle(sketch, "E3.0.19.42", {"center": v(-246.44, -567.04) * mm, "radius": 3 * mm});
            skCircle(sketch, "E3.0.19.44", {"center": v(32.96, -567.04) * mm, "radius": 3 * mm});
            skCircle(sketch, "E3.0.19.45", {"center": v(-195.64, -567.04) * mm, "radius": 3 * mm});
            skCircle(sketch, "E3.0.19.47", {"center": v(-322.64, -567.04) * mm, "radius": 3 * mm});
            skCircle(sketch, "E3.0.19.49", {"center": v(-17.84, -567.04) * mm, "radius": 3 * mm});
            skCircle(sketch, "E3.0.19.50", {"center": v(134.56, -567.04) * mm, "radius": 3 * mm});
            skCircle(sketch, "E3.0.19.51", {"center": v(-449.64, -567.04) * mm, "radius": 3 * mm});
            skCircle(sketch, "E3.0.19.53", {"center": v(-170.24, -567.04) * mm, "radius": 3 * mm});
            skCircle(sketch, "E3.0.19.54", {"center": v(-119.44, -567.04) * mm, "radius": 3 * mm});
            skCircle(sketch, "E3.0.19.55", {"center": v(-373.44, -567.04) * mm, "radius": 3 * mm});
            skCircle(sketch, "E3.0.19.56", {"center": v(109.16, -567.04) * mm, "radius": 3 * mm});
            skCircle(sketch, "E3.0.19.57", {"center": v(-424.24, -567.04) * mm, "radius": 3 * mm});
            skCircle(sketch, "E3.0.19.58", {"center": v(-525.84, -567.04) * mm, "radius": 3 * mm});
            skCircle(sketch, "E3.0.19.59", {"center": v(-94.04, -567.04) * mm, "radius": 3 * mm});
            skCircle(sketch, "E3.0.19.60", {"center": v(-475.04, -567.04) * mm, "radius": 3 * mm});
            skCircle(sketch, "E3.0.19.61", {"center": v(58.36, -567.04) * mm, "radius": 3 * mm});
            skCircle(sketch, "E3.0.19.63", {"center": v(7.56, -567.04) * mm, "radius": 3 * mm});
            skCircle(sketch, "E3.0.19.64", {"center": v(-297.24, -567.04) * mm, "radius": 3 * mm});
            skCircle(sketch, "E3.0.19.67", {"center": v(-144.84, -567.04) * mm, "radius": 3 * mm});
            skCircle(sketch, "E3.0.19.68", {"center": v(-221.04, -567.04) * mm, "radius": 3 * mm});
            skCircle(sketch, "E3.0.19.69", {"center": v(-271.84, -567.04) * mm, "radius": 3 * mm});
            skCircle(sketch, "E3.0.19.70", {"center": v(83.76, -567.04) * mm, "radius": 3 * mm});
            skCircle(sketch, "E3.0.19.71", {"center": v(134.56, -567.04) * mm, "radius": 3 * mm});
            skCircle(sketch, "E3.0.19.72", {"center": v(-424.24, -567.04) * mm, "radius": 3 * mm});
            skCircle(sketch, "E3.0.19.73", {"center": v(-195.64, -567.04) * mm, "radius": 3 * mm});
            skCircle(sketch, "E3.0.19.74", {"center": v(-525.84, -567.04) * mm, "radius": 3 * mm});
            skCircle(sketch, "E3.0.19.75", {"center": v(109.16, -567.04) * mm, "radius": 3 * mm});
            skCircle(sketch, "E3.0.19.76", {"center": v(-246.44, -567.04) * mm, "radius": 3 * mm});
            skCircle(sketch, "E3.0.19.77", {"center": v(-449.64, -567.04) * mm, "radius": 3 * mm});
            skCircle(sketch, "E3.0.19.78", {"center": v(-144.84, -567.04) * mm, "radius": 3 * mm});
            skCircle(sketch, "E3.0.19.79", {"center": v(-348.04, -567.04) * mm, "radius": 3 * mm});
            skCircle(sketch, "E3.0.19.80", {"center": v(-94.04, -567.04) * mm, "radius": 3 * mm});
            skCircle(sketch, "E3.0.19.81", {"center": v(32.96, -567.04) * mm, "radius": 3 * mm});
            skCircle(sketch, "E3.0.19.82", {"center": v(-68.64, -567.04) * mm, "radius": 3 * mm});
            skCircle(sketch, "E3.0.19.84", {"center": v(-373.44, -567.04) * mm, "radius": 3 * mm});
            skCircle(sketch, "E3.0.19.86", {"center": v(-170.24, -567.04) * mm, "radius": 3 * mm});
            skCircle(sketch, "E3.0.19.88", {"center": v(-17.84, -567.04) * mm, "radius": 3 * mm});
            skCircle(sketch, "E3.0.19.89", {"center": v(-221.04, -567.04) * mm, "radius": 3 * mm});
            skCircle(sketch, "E3.0.19.90", {"center": v(-119.44, -567.04) * mm, "radius": 3 * mm});
            skCircle(sketch, "E3.0.19.92", {"center": v(-475.04, -567.04) * mm, "radius": 3 * mm});
            skCircle(sketch, "E3.0.19.93", {"center": v(-297.24, -567.04) * mm, "radius": 3 * mm});
            skCircle(sketch, "E3.0.19.94", {"center": v(-43.24, -567.04) * mm, "radius": 3 * mm});
            skCircle(sketch, "E3.0.19.95", {"center": v(83.76, -567.04) * mm, "radius": 3 * mm});
            skCircle(sketch, "E3.0.19.97", {"center": v(-500.44, -567.04) * mm, "radius": 3 * mm});
            skCircle(sketch, "E3.0.19.98", {"center": v(-322.64, -567.04) * mm, "radius": 3 * mm});
            skCircle(sketch, "E3.0.19.100", {"center": v(-398.84, -567.04) * mm, "radius": 3 * mm});
            skCircle(sketch, "E3.0.19.102", {"center": v(58.36, -567.04) * mm, "radius": 3 * mm});
            skCircle(sketch, "E3.0.19.103", {"center": v(7.56, -567.04) * mm, "radius": 3 * mm});
            skCircle(sketch, "E3.0.19.104", {"center": v(-271.84, -567.04) * mm, "radius": 3 * mm});
            skCircle(sketch, "E3.0.20.2", {"center": v(-475.04, -592.44) * mm, "radius": 3 * mm});
            skCircle(sketch, "E3.0.20.4", {"center": v(-297.24, -592.44) * mm, "radius": 3 * mm});
            skCircle(sketch, "E3.0.20.5", {"center": v(-246.44, -592.44) * mm, "radius": 3 * mm});
            skCircle(sketch, "E3.0.20.6", {"center": v(-373.44, -592.44) * mm, "radius": 3 * mm});
            skCircle(sketch, "E3.0.20.7", {"center": v(-94.04, -592.44) * mm, "radius": 3 * mm});
            skCircle(sketch, "E3.0.20.8", {"center": v(-348.04, -592.44) * mm, "radius": 3 * mm});
            skCircle(sketch, "E3.0.20.9", {"center": v(-144.84, -592.44) * mm, "radius": 3 * mm});
            skCircle(sketch, "E3.0.20.11", {"center": v(-424.24, -592.44) * mm, "radius": 3 * mm});
            skCircle(sketch, "E3.0.20.12", {"center": v(7.56, -592.44) * mm, "radius": 3 * mm});
            skCircle(sketch, "E3.0.20.15", {"center": v(134.56, -592.44) * mm, "radius": 3 * mm});
            skCircle(sketch, "E3.0.20.17", {"center": v(109.16, -592.44) * mm, "radius": 3 * mm});
            skCircle(sketch, "E3.0.20.18", {"center": v(-119.44, -592.44) * mm, "radius": 3 * mm});
            skCircle(sketch, "E3.0.20.20", {"center": v(83.76, -592.44) * mm, "radius": 3 * mm});
            skCircle(sketch, "E3.0.20.21", {"center": v(-500.44, -592.44) * mm, "radius": 3 * mm});
            skCircle(sketch, "E3.0.20.22", {"center": v(58.36, -592.44) * mm, "radius": 3 * mm});
            skCircle(sketch, "E3.0.20.23", {"center": v(-525.84, -592.44) * mm, "radius": 3 * mm});
            skCircle(sketch, "E3.0.20.24", {"center": v(-17.84, -592.44) * mm, "radius": 3 * mm});
            skCircle(sketch, "E3.0.20.25", {"center": v(-398.84, -592.44) * mm, "radius": 3 * mm});
            skCircle(sketch, "E3.0.20.27", {"center": v(-43.24, -592.44) * mm, "radius": 3 * mm});
            skCircle(sketch, "E3.0.20.28", {"center": v(-68.64, -592.44) * mm, "radius": 3 * mm});
            skCircle(sketch, "E3.0.20.29", {"center": v(-322.64, -592.44) * mm, "radius": 3 * mm});
            skCircle(sketch, "E3.0.20.30", {"center": v(-221.04, -592.44) * mm, "radius": 3 * mm});
            skCircle(sketch, "E3.0.20.31", {"center": v(-195.64, -592.44) * mm, "radius": 3 * mm});
            skCircle(sketch, "E3.0.20.32", {"center": v(-170.24, -592.44) * mm, "radius": 3 * mm});
            skCircle(sketch, "E3.0.20.34", {"center": v(-449.64, -592.44) * mm, "radius": 3 * mm});
            skCircle(sketch, "E3.0.20.35", {"center": v(-271.84, -592.44) * mm, "radius": 3 * mm});
            skCircle(sketch, "E3.0.20.36", {"center": v(32.96, -592.44) * mm, "radius": 3 * mm});
            skCircle(sketch, "E3.0.20.37", {"center": v(-500.44, -592.44) * mm, "radius": 3 * mm});
            skCircle(sketch, "E3.0.20.38", {"center": v(-43.24, -592.44) * mm, "radius": 3 * mm});
            skCircle(sketch, "E3.0.20.39", {"center": v(-348.04, -592.44) * mm, "radius": 3 * mm});
            skCircle(sketch, "E3.0.20.40", {"center": v(-68.64, -592.44) * mm, "radius": 3 * mm});
            skCircle(sketch, "E3.0.20.41", {"center": v(-398.84, -592.44) * mm, "radius": 3 * mm});
            skCircle(sketch, "E3.0.20.42", {"center": v(-246.44, -592.44) * mm, "radius": 3 * mm});
            skCircle(sketch, "E3.0.20.44", {"center": v(32.96, -592.44) * mm, "radius": 3 * mm});
            skCircle(sketch, "E3.0.20.45", {"center": v(-195.64, -592.44) * mm, "radius": 3 * mm});
            skCircle(sketch, "E3.0.20.47", {"center": v(-322.64, -592.44) * mm, "radius": 3 * mm});
            skCircle(sketch, "E3.0.20.49", {"center": v(-17.84, -592.44) * mm, "radius": 3 * mm});
            skCircle(sketch, "E3.0.20.50", {"center": v(134.56, -592.44) * mm, "radius": 3 * mm});
            skCircle(sketch, "E3.0.20.51", {"center": v(-449.64, -592.44) * mm, "radius": 3 * mm});
            skCircle(sketch, "E3.0.20.53", {"center": v(-170.24, -592.44) * mm, "radius": 3 * mm});
            skCircle(sketch, "E3.0.20.54", {"center": v(-119.44, -592.44) * mm, "radius": 3 * mm});
            skCircle(sketch, "E3.0.20.55", {"center": v(-373.44, -592.44) * mm, "radius": 3 * mm});
            skCircle(sketch, "E3.0.20.56", {"center": v(109.16, -592.44) * mm, "radius": 3 * mm});
            skCircle(sketch, "E3.0.20.57", {"center": v(-424.24, -592.44) * mm, "radius": 3 * mm});
            skCircle(sketch, "E3.0.20.58", {"center": v(-525.84, -592.44) * mm, "radius": 3 * mm});
            skCircle(sketch, "E3.0.20.59", {"center": v(-94.04, -592.44) * mm, "radius": 3 * mm});
            skCircle(sketch, "E3.0.20.60", {"center": v(-475.04, -592.44) * mm, "radius": 3 * mm});
            skCircle(sketch, "E3.0.20.61", {"center": v(58.36, -592.44) * mm, "radius": 3 * mm});
            skCircle(sketch, "E3.0.20.63", {"center": v(7.56, -592.44) * mm, "radius": 3 * mm});
            skCircle(sketch, "E3.0.20.64", {"center": v(-297.24, -592.44) * mm, "radius": 3 * mm});
            skCircle(sketch, "E3.0.20.67", {"center": v(-144.84, -592.44) * mm, "radius": 3 * mm});
            skCircle(sketch, "E3.0.20.68", {"center": v(-221.04, -592.44) * mm, "radius": 3 * mm});
            skCircle(sketch, "E3.0.20.69", {"center": v(-271.84, -592.44) * mm, "radius": 3 * mm});
            skCircle(sketch, "E3.0.20.70", {"center": v(83.76, -592.44) * mm, "radius": 3 * mm});
            skCircle(sketch, "E3.0.20.71", {"center": v(134.56, -592.44) * mm, "radius": 3 * mm});
            skCircle(sketch, "E3.0.20.72", {"center": v(-424.24, -592.44) * mm, "radius": 3 * mm});
            skCircle(sketch, "E3.0.20.73", {"center": v(-195.64, -592.44) * mm, "radius": 3 * mm});
            skCircle(sketch, "E3.0.20.74", {"center": v(-525.84, -592.44) * mm, "radius": 3 * mm});
            skCircle(sketch, "E3.0.20.75", {"center": v(109.16, -592.44) * mm, "radius": 3 * mm});
            skCircle(sketch, "E3.0.20.76", {"center": v(-246.44, -592.44) * mm, "radius": 3 * mm});
            skCircle(sketch, "E3.0.20.77", {"center": v(-449.64, -592.44) * mm, "radius": 3 * mm});
            skCircle(sketch, "E3.0.20.78", {"center": v(-144.84, -592.44) * mm, "radius": 3 * mm});
            skCircle(sketch, "E3.0.20.79", {"center": v(-348.04, -592.44) * mm, "radius": 3 * mm});
            skCircle(sketch, "E3.0.20.80", {"center": v(-94.04, -592.44) * mm, "radius": 3 * mm});
            skCircle(sketch, "E3.0.20.81", {"center": v(32.96, -592.44) * mm, "radius": 3 * mm});
            skCircle(sketch, "E3.0.20.82", {"center": v(-68.64, -592.44) * mm, "radius": 3 * mm});
            skCircle(sketch, "E3.0.20.84", {"center": v(-373.44, -592.44) * mm, "radius": 3 * mm});
            skCircle(sketch, "E3.0.20.86", {"center": v(-170.24, -592.44) * mm, "radius": 3 * mm});
            skCircle(sketch, "E3.0.20.88", {"center": v(-17.84, -592.44) * mm, "radius": 3 * mm});
            skCircle(sketch, "E3.0.20.89", {"center": v(-221.04, -592.44) * mm, "radius": 3 * mm});
            skCircle(sketch, "E3.0.20.90", {"center": v(-119.44, -592.44) * mm, "radius": 3 * mm});
            skCircle(sketch, "E3.0.20.92", {"center": v(-475.04, -592.44) * mm, "radius": 3 * mm});
            skCircle(sketch, "E3.0.20.93", {"center": v(-297.24, -592.44) * mm, "radius": 3 * mm});
            skCircle(sketch, "E3.0.20.94", {"center": v(-43.24, -592.44) * mm, "radius": 3 * mm});
            skCircle(sketch, "E3.0.20.95", {"center": v(83.76, -592.44) * mm, "radius": 3 * mm});
            skCircle(sketch, "E3.0.20.97", {"center": v(-500.44, -592.44) * mm, "radius": 3 * mm});
            skCircle(sketch, "E3.0.20.98", {"center": v(-322.64, -592.44) * mm, "radius": 3 * mm});
            skCircle(sketch, "E3.0.20.100", {"center": v(-398.84, -592.44) * mm, "radius": 3 * mm});
            skCircle(sketch, "E3.0.20.102", {"center": v(58.36, -592.44) * mm, "radius": 3 * mm});
            skCircle(sketch, "E3.0.20.103", {"center": v(7.56, -592.44) * mm, "radius": 3 * mm});
            skCircle(sketch, "E3.0.20.104", {"center": v(-271.84, -592.44) * mm, "radius": 3 * mm});
            skCircle(sketch, "E3.0.21.2", {"center": v(-475.04, -617.84) * mm, "radius": 3 * mm});
            skCircle(sketch, "E3.0.21.4", {"center": v(-297.24, -617.84) * mm, "radius": 3 * mm});
            skCircle(sketch, "E3.0.21.5", {"center": v(-246.44, -617.84) * mm, "radius": 3 * mm});
            skCircle(sketch, "E3.0.21.6", {"center": v(-373.44, -617.84) * mm, "radius": 3 * mm});
            skCircle(sketch, "E3.0.21.7", {"center": v(-94.04, -617.84) * mm, "radius": 3 * mm});
            skCircle(sketch, "E3.0.21.8", {"center": v(-348.04, -617.84) * mm, "radius": 3 * mm});
            skCircle(sketch, "E3.0.21.9", {"center": v(-144.84, -617.84) * mm, "radius": 3 * mm});
            skCircle(sketch, "E3.0.21.11", {"center": v(-424.24, -617.84) * mm, "radius": 3 * mm});
            skCircle(sketch, "E3.0.21.12", {"center": v(7.56, -617.84) * mm, "radius": 3 * mm});
            skCircle(sketch, "E3.0.21.15", {"center": v(134.56, -617.84) * mm, "radius": 3 * mm});
            skCircle(sketch, "E3.0.21.17", {"center": v(109.16, -617.84) * mm, "radius": 3 * mm});
            skCircle(sketch, "E3.0.21.18", {"center": v(-119.44, -617.84) * mm, "radius": 3 * mm});
            skCircle(sketch, "E3.0.21.20", {"center": v(83.76, -617.84) * mm, "radius": 3 * mm});
            skCircle(sketch, "E3.0.21.21", {"center": v(-500.44, -617.84) * mm, "radius": 3 * mm});
            skCircle(sketch, "E3.0.21.22", {"center": v(58.36, -617.84) * mm, "radius": 3 * mm});
            skCircle(sketch, "E3.0.21.23", {"center": v(-525.84, -617.84) * mm, "radius": 3 * mm});
            skCircle(sketch, "E3.0.21.24", {"center": v(-17.84, -617.84) * mm, "radius": 3 * mm});
            skCircle(sketch, "E3.0.21.25", {"center": v(-398.84, -617.84) * mm, "radius": 3 * mm});
            skCircle(sketch, "E3.0.21.27", {"center": v(-43.24, -617.84) * mm, "radius": 3 * mm});
            skCircle(sketch, "E3.0.21.28", {"center": v(-68.64, -617.84) * mm, "radius": 3 * mm});
            skCircle(sketch, "E3.0.21.29", {"center": v(-322.64, -617.84) * mm, "radius": 3 * mm});
            skCircle(sketch, "E3.0.21.30", {"center": v(-221.04, -617.84) * mm, "radius": 3 * mm});
            skCircle(sketch, "E3.0.21.31", {"center": v(-195.64, -617.84) * mm, "radius": 3 * mm});
            skCircle(sketch, "E3.0.21.32", {"center": v(-170.24, -617.84) * mm, "radius": 3 * mm});
            skCircle(sketch, "E3.0.21.34", {"center": v(-449.64, -617.84) * mm, "radius": 3 * mm});
            skCircle(sketch, "E3.0.21.35", {"center": v(-271.84, -617.84) * mm, "radius": 3 * mm});
            skCircle(sketch, "E3.0.21.36", {"center": v(32.96, -617.84) * mm, "radius": 3 * mm});
            skCircle(sketch, "E3.0.21.37", {"center": v(-500.44, -617.84) * mm, "radius": 3 * mm});
            skCircle(sketch, "E3.0.21.38", {"center": v(-43.24, -617.84) * mm, "radius": 3 * mm});
            skCircle(sketch, "E3.0.21.39", {"center": v(-348.04, -617.84) * mm, "radius": 3 * mm});
            skCircle(sketch, "E3.0.21.40", {"center": v(-68.64, -617.84) * mm, "radius": 3 * mm});
            skCircle(sketch, "E3.0.21.41", {"center": v(-398.84, -617.84) * mm, "radius": 3 * mm});
            skCircle(sketch, "E3.0.21.42", {"center": v(-246.44, -617.84) * mm, "radius": 3 * mm});
            skCircle(sketch, "E3.0.21.44", {"center": v(32.96, -617.84) * mm, "radius": 3 * mm});
            skCircle(sketch, "E3.0.21.45", {"center": v(-195.64, -617.84) * mm, "radius": 3 * mm});
            skCircle(sketch, "E3.0.21.47", {"center": v(-322.64, -617.84) * mm, "radius": 3 * mm});
            skCircle(sketch, "E3.0.21.49", {"center": v(-17.84, -617.84) * mm, "radius": 3 * mm});
            skCircle(sketch, "E3.0.21.50", {"center": v(134.56, -617.84) * mm, "radius": 3 * mm});
            skCircle(sketch, "E3.0.21.51", {"center": v(-449.64, -617.84) * mm, "radius": 3 * mm});
            skCircle(sketch, "E3.0.21.53", {"center": v(-170.24, -617.84) * mm, "radius": 3 * mm});
            skCircle(sketch, "E3.0.21.54", {"center": v(-119.44, -617.84) * mm, "radius": 3 * mm});
            skCircle(sketch, "E3.0.21.55", {"center": v(-373.44, -617.84) * mm, "radius": 3 * mm});
            skCircle(sketch, "E3.0.21.56", {"center": v(109.16, -617.84) * mm, "radius": 3 * mm});
            skCircle(sketch, "E3.0.21.57", {"center": v(-424.24, -617.84) * mm, "radius": 3 * mm});
            skCircle(sketch, "E3.0.21.58", {"center": v(-525.84, -617.84) * mm, "radius": 3 * mm});
            skCircle(sketch, "E3.0.21.59", {"center": v(-94.04, -617.84) * mm, "radius": 3 * mm});
            skCircle(sketch, "E3.0.21.60", {"center": v(-475.04, -617.84) * mm, "radius": 3 * mm});
            skCircle(sketch, "E3.0.21.61", {"center": v(58.36, -617.84) * mm, "radius": 3 * mm});
            skCircle(sketch, "E3.0.21.63", {"center": v(7.56, -617.84) * mm, "radius": 3 * mm});
            skCircle(sketch, "E3.0.21.64", {"center": v(-297.24, -617.84) * mm, "radius": 3 * mm});
            skCircle(sketch, "E3.0.21.67", {"center": v(-144.84, -617.84) * mm, "radius": 3 * mm});
            skCircle(sketch, "E3.0.21.68", {"center": v(-221.04, -617.84) * mm, "radius": 3 * mm});
            skCircle(sketch, "E3.0.21.69", {"center": v(-271.84, -617.84) * mm, "radius": 3 * mm});
            skCircle(sketch, "E3.0.21.70", {"center": v(83.76, -617.84) * mm, "radius": 3 * mm});
            skCircle(sketch, "E3.0.21.71", {"center": v(134.56, -617.84) * mm, "radius": 3 * mm});
            skCircle(sketch, "E3.0.21.72", {"center": v(-424.24, -617.84) * mm, "radius": 3 * mm});
            skCircle(sketch, "E3.0.21.73", {"center": v(-195.64, -617.84) * mm, "radius": 3 * mm});
            skCircle(sketch, "E3.0.21.74", {"center": v(-525.84, -617.84) * mm, "radius": 3 * mm});
            skCircle(sketch, "E3.0.21.75", {"center": v(109.16, -617.84) * mm, "radius": 3 * mm});
            skCircle(sketch, "E3.0.21.76", {"center": v(-246.44, -617.84) * mm, "radius": 3 * mm});
            skCircle(sketch, "E3.0.21.77", {"center": v(-449.64, -617.84) * mm, "radius": 3 * mm});
            skCircle(sketch, "E3.0.21.78", {"center": v(-144.84, -617.84) * mm, "radius": 3 * mm});
            skCircle(sketch, "E3.0.21.79", {"center": v(-348.04, -617.84) * mm, "radius": 3 * mm});
            skCircle(sketch, "E3.0.21.80", {"center": v(-94.04, -617.84) * mm, "radius": 3 * mm});
            skCircle(sketch, "E3.0.21.81", {"center": v(32.96, -617.84) * mm, "radius": 3 * mm});
            skCircle(sketch, "E3.0.21.82", {"center": v(-68.64, -617.84) * mm, "radius": 3 * mm});
            skCircle(sketch, "E3.0.21.84", {"center": v(-373.44, -617.84) * mm, "radius": 3 * mm});
            skCircle(sketch, "E3.0.21.86", {"center": v(-170.24, -617.84) * mm, "radius": 3 * mm});
            skCircle(sketch, "E3.0.21.88", {"center": v(-17.84, -617.84) * mm, "radius": 3 * mm});
            skCircle(sketch, "E3.0.21.89", {"center": v(-221.04, -617.84) * mm, "radius": 3 * mm});
            skCircle(sketch, "E3.0.21.90", {"center": v(-119.44, -617.84) * mm, "radius": 3 * mm});
            skCircle(sketch, "E3.0.21.92", {"center": v(-475.04, -617.84) * mm, "radius": 3 * mm});
            skCircle(sketch, "E3.0.21.93", {"center": v(-297.24, -617.84) * mm, "radius": 3 * mm});
            skCircle(sketch, "E3.0.21.94", {"center": v(-43.24, -617.84) * mm, "radius": 3 * mm});
            skCircle(sketch, "E3.0.21.95", {"center": v(83.76, -617.84) * mm, "radius": 3 * mm});
            skCircle(sketch, "E3.0.21.97", {"center": v(-500.44, -617.84) * mm, "radius": 3 * mm});
            skCircle(sketch, "E3.0.21.98", {"center": v(-322.64, -617.84) * mm, "radius": 3 * mm});
            skCircle(sketch, "E3.0.21.100", {"center": v(-398.84, -617.84) * mm, "radius": 3 * mm});
            skCircle(sketch, "E3.0.21.102", {"center": v(58.36, -617.84) * mm, "radius": 3 * mm});
            skCircle(sketch, "E3.0.21.103", {"center": v(7.56, -617.84) * mm, "radius": 3 * mm});
            skCircle(sketch, "E3.0.21.104", {"center": v(-271.84, -617.84) * mm, "radius": 3 * mm});
            skCircle(sketch, "E3.0.22.2", {"center": v(-475.04, -643.24) * mm, "radius": 3 * mm});
            skCircle(sketch, "E3.0.22.4", {"center": v(-297.24, -643.24) * mm, "radius": 3 * mm});
            skCircle(sketch, "E3.0.22.5", {"center": v(-246.44, -643.24) * mm, "radius": 3 * mm});
            skCircle(sketch, "E3.0.22.6", {"center": v(-373.44, -643.24) * mm, "radius": 3 * mm});
            skCircle(sketch, "E3.0.22.7", {"center": v(-94.04, -643.24) * mm, "radius": 3 * mm});
            skCircle(sketch, "E3.0.22.8", {"center": v(-348.04, -643.24) * mm, "radius": 3 * mm});
            skCircle(sketch, "E3.0.22.9", {"center": v(-144.84, -643.24) * mm, "radius": 3 * mm});
            skCircle(sketch, "E3.0.22.11", {"center": v(-424.24, -643.24) * mm, "radius": 3 * mm});
            skCircle(sketch, "E3.0.22.12", {"center": v(7.56, -643.24) * mm, "radius": 3 * mm});
            skCircle(sketch, "E3.0.22.15", {"center": v(134.56, -643.24) * mm, "radius": 3 * mm});
            skCircle(sketch, "E3.0.22.17", {"center": v(109.16, -643.24) * mm, "radius": 3 * mm});
            skCircle(sketch, "E3.0.22.18", {"center": v(-119.44, -643.24) * mm, "radius": 3 * mm});
            skCircle(sketch, "E3.0.22.20", {"center": v(83.76, -643.24) * mm, "radius": 3 * mm});
            skCircle(sketch, "E3.0.22.21", {"center": v(-500.44, -643.24) * mm, "radius": 3 * mm});
            skCircle(sketch, "E3.0.22.22", {"center": v(58.36, -643.24) * mm, "radius": 3 * mm});
            skCircle(sketch, "E3.0.22.23", {"center": v(-525.84, -643.24) * mm, "radius": 3 * mm});
            skCircle(sketch, "E3.0.22.24", {"center": v(-17.84, -643.24) * mm, "radius": 3 * mm});
            skCircle(sketch, "E3.0.22.25", {"center": v(-398.84, -643.24) * mm, "radius": 3 * mm});
            skCircle(sketch, "E3.0.22.27", {"center": v(-43.24, -643.24) * mm, "radius": 3 * mm});
            skCircle(sketch, "E3.0.22.28", {"center": v(-68.64, -643.24) * mm, "radius": 3 * mm});
            skCircle(sketch, "E3.0.22.29", {"center": v(-322.64, -643.24) * mm, "radius": 3 * mm});
            skCircle(sketch, "E3.0.22.30", {"center": v(-221.04, -643.24) * mm, "radius": 3 * mm});
            skCircle(sketch, "E3.0.22.31", {"center": v(-195.64, -643.24) * mm, "radius": 3 * mm});
            skCircle(sketch, "E3.0.22.32", {"center": v(-170.24, -643.24) * mm, "radius": 3 * mm});
            skCircle(sketch, "E3.0.22.34", {"center": v(-449.64, -643.24) * mm, "radius": 3 * mm});
            skCircle(sketch, "E3.0.22.35", {"center": v(-271.84, -643.24) * mm, "radius": 3 * mm});
            skCircle(sketch, "E3.0.22.36", {"center": v(32.96, -643.24) * mm, "radius": 3 * mm});
            skCircle(sketch, "E3.0.22.37", {"center": v(-500.44, -643.24) * mm, "radius": 3 * mm});
            skCircle(sketch, "E3.0.22.38", {"center": v(-43.24, -643.24) * mm, "radius": 3 * mm});
            skCircle(sketch, "E3.0.22.39", {"center": v(-348.04, -643.24) * mm, "radius": 3 * mm});
            skCircle(sketch, "E3.0.22.40", {"center": v(-68.64, -643.24) * mm, "radius": 3 * mm});
            skCircle(sketch, "E3.0.22.41", {"center": v(-398.84, -643.24) * mm, "radius": 3 * mm});
            skCircle(sketch, "E3.0.22.42", {"center": v(-246.44, -643.24) * mm, "radius": 3 * mm});
            skCircle(sketch, "E3.0.22.44", {"center": v(32.96, -643.24) * mm, "radius": 3 * mm});
            skCircle(sketch, "E3.0.22.45", {"center": v(-195.64, -643.24) * mm, "radius": 3 * mm});
            skCircle(sketch, "E3.0.22.47", {"center": v(-322.64, -643.24) * mm, "radius": 3 * mm});
            skCircle(sketch, "E3.0.22.49", {"center": v(-17.84, -643.24) * mm, "radius": 3 * mm});
            skCircle(sketch, "E3.0.22.50", {"center": v(134.56, -643.24) * mm, "radius": 3 * mm});
            skCircle(sketch, "E3.0.22.51", {"center": v(-449.64, -643.24) * mm, "radius": 3 * mm});
            skCircle(sketch, "E3.0.22.53", {"center": v(-170.24, -643.24) * mm, "radius": 3 * mm});
            skCircle(sketch, "E3.0.22.54", {"center": v(-119.44, -643.24) * mm, "radius": 3 * mm});
            skCircle(sketch, "E3.0.22.55", {"center": v(-373.44, -643.24) * mm, "radius": 3 * mm});
            skCircle(sketch, "E3.0.22.56", {"center": v(109.16, -643.24) * mm, "radius": 3 * mm});
            skCircle(sketch, "E3.0.22.57", {"center": v(-424.24, -643.24) * mm, "radius": 3 * mm});
            skCircle(sketch, "E3.0.22.58", {"center": v(-525.84, -643.24) * mm, "radius": 3 * mm});
            skCircle(sketch, "E3.0.22.59", {"center": v(-94.04, -643.24) * mm, "radius": 3 * mm});
            skCircle(sketch, "E3.0.22.60", {"center": v(-475.04, -643.24) * mm, "radius": 3 * mm});
            skCircle(sketch, "E3.0.22.61", {"center": v(58.36, -643.24) * mm, "radius": 3 * mm});
            skCircle(sketch, "E3.0.22.63", {"center": v(7.56, -643.24) * mm, "radius": 3 * mm});
            skCircle(sketch, "E3.0.22.64", {"center": v(-297.24, -643.24) * mm, "radius": 3 * mm});
            skCircle(sketch, "E3.0.22.67", {"center": v(-144.84, -643.24) * mm, "radius": 3 * mm});
            skCircle(sketch, "E3.0.22.68", {"center": v(-221.04, -643.24) * mm, "radius": 3 * mm});
            skCircle(sketch, "E3.0.22.69", {"center": v(-271.84, -643.24) * mm, "radius": 3 * mm});
            skCircle(sketch, "E3.0.22.70", {"center": v(83.76, -643.24) * mm, "radius": 3 * mm});
            skCircle(sketch, "E3.0.22.71", {"center": v(134.56, -643.24) * mm, "radius": 3 * mm});
            skCircle(sketch, "E3.0.22.72", {"center": v(-424.24, -643.24) * mm, "radius": 3 * mm});
            skCircle(sketch, "E3.0.22.73", {"center": v(-195.64, -643.24) * mm, "radius": 3 * mm});
            skCircle(sketch, "E3.0.22.74", {"center": v(-525.84, -643.24) * mm, "radius": 3 * mm});
            skCircle(sketch, "E3.0.22.75", {"center": v(109.16, -643.24) * mm, "radius": 3 * mm});
            skCircle(sketch, "E3.0.22.76", {"center": v(-246.44, -643.24) * mm, "radius": 3 * mm});
            skCircle(sketch, "E3.0.22.77", {"center": v(-449.64, -643.24) * mm, "radius": 3 * mm});
            skCircle(sketch, "E3.0.22.78", {"center": v(-144.84, -643.24) * mm, "radius": 3 * mm});
            skCircle(sketch, "E3.0.22.79", {"center": v(-348.04, -643.24) * mm, "radius": 3 * mm});
            skCircle(sketch, "E3.0.22.80", {"center": v(-94.04, -643.24) * mm, "radius": 3 * mm});
            skCircle(sketch, "E3.0.22.81", {"center": v(32.96, -643.24) * mm, "radius": 3 * mm});
            skCircle(sketch, "E3.0.22.82", {"center": v(-68.64, -643.24) * mm, "radius": 3 * mm});
            skCircle(sketch, "E3.0.22.84", {"center": v(-373.44, -643.24) * mm, "radius": 3 * mm});
            skCircle(sketch, "E3.0.22.86", {"center": v(-170.24, -643.24) * mm, "radius": 3 * mm});
            skCircle(sketch, "E3.0.22.88", {"center": v(-17.84, -643.24) * mm, "radius": 3 * mm});
            skCircle(sketch, "E3.0.22.89", {"center": v(-221.04, -643.24) * mm, "radius": 3 * mm});
            skCircle(sketch, "E3.0.22.90", {"center": v(-119.44, -643.24) * mm, "radius": 3 * mm});
            skCircle(sketch, "E3.0.22.92", {"center": v(-475.04, -643.24) * mm, "radius": 3 * mm});
            skCircle(sketch, "E3.0.22.93", {"center": v(-297.24, -643.24) * mm, "radius": 3 * mm});
            skCircle(sketch, "E3.0.22.94", {"center": v(-43.24, -643.24) * mm, "radius": 3 * mm});
            skCircle(sketch, "E3.0.22.95", {"center": v(83.76, -643.24) * mm, "radius": 3 * mm});
            skCircle(sketch, "E3.0.22.97", {"center": v(-500.44, -643.24) * mm, "radius": 3 * mm});
            skCircle(sketch, "E3.0.22.98", {"center": v(-322.64, -643.24) * mm, "radius": 3 * mm});
            skCircle(sketch, "E3.0.22.100", {"center": v(-398.84, -643.24) * mm, "radius": 3 * mm});
            skCircle(sketch, "E3.0.22.102", {"center": v(58.36, -643.24) * mm, "radius": 3 * mm});
            skCircle(sketch, "E3.0.22.103", {"center": v(7.56, -643.24) * mm, "radius": 3 * mm});
            skCircle(sketch, "E3.0.22.104", {"center": v(-271.84, -643.24) * mm, "radius": 3 * mm});
            skCircle(sketch, "E3.0.23.2", {"center": v(-475.04, -668.64) * mm, "radius": 3 * mm});
            skCircle(sketch, "E3.0.23.4", {"center": v(-297.24, -668.64) * mm, "radius": 3 * mm});
            skCircle(sketch, "E3.0.23.5", {"center": v(-246.44, -668.64) * mm, "radius": 3 * mm});
            skCircle(sketch, "E3.0.23.6", {"center": v(-373.44, -668.64) * mm, "radius": 3 * mm});
            skCircle(sketch, "E3.0.23.7", {"center": v(-94.04, -668.64) * mm, "radius": 3 * mm});
            skCircle(sketch, "E3.0.23.8", {"center": v(-348.04, -668.64) * mm, "radius": 3 * mm});
            skCircle(sketch, "E3.0.23.9", {"center": v(-144.84, -668.64) * mm, "radius": 3 * mm});
            skCircle(sketch, "E3.0.23.11", {"center": v(-424.24, -668.64) * mm, "radius": 3 * mm});
            skCircle(sketch, "E3.0.23.12", {"center": v(7.56, -668.64) * mm, "radius": 3 * mm});
            skCircle(sketch, "E3.0.23.15", {"center": v(134.56, -668.64) * mm, "radius": 3 * mm});
            skCircle(sketch, "E3.0.23.17", {"center": v(109.16, -668.64) * mm, "radius": 3 * mm});
            skCircle(sketch, "E3.0.23.18", {"center": v(-119.44, -668.64) * mm, "radius": 3 * mm});
            skCircle(sketch, "E3.0.23.20", {"center": v(83.76, -668.64) * mm, "radius": 3 * mm});
            skCircle(sketch, "E3.0.23.21", {"center": v(-500.44, -668.64) * mm, "radius": 3 * mm});
            skCircle(sketch, "E3.0.23.22", {"center": v(58.36, -668.64) * mm, "radius": 3 * mm});
            skCircle(sketch, "E3.0.23.23", {"center": v(-525.84, -668.64) * mm, "radius": 3 * mm});
            skCircle(sketch, "E3.0.23.24", {"center": v(-17.84, -668.64) * mm, "radius": 3 * mm});
            skCircle(sketch, "E3.0.23.25", {"center": v(-398.84, -668.64) * mm, "radius": 3 * mm});
            skCircle(sketch, "E3.0.23.27", {"center": v(-43.24, -668.64) * mm, "radius": 3 * mm});
            skCircle(sketch, "E3.0.23.28", {"center": v(-68.64, -668.64) * mm, "radius": 3 * mm});
            skCircle(sketch, "E3.0.23.29", {"center": v(-322.64, -668.64) * mm, "radius": 3 * mm});
            skCircle(sketch, "E3.0.23.30", {"center": v(-221.04, -668.64) * mm, "radius": 3 * mm});
            skCircle(sketch, "E3.0.23.31", {"center": v(-195.64, -668.64) * mm, "radius": 3 * mm});
            skCircle(sketch, "E3.0.23.32", {"center": v(-170.24, -668.64) * mm, "radius": 3 * mm});
            skCircle(sketch, "E3.0.23.34", {"center": v(-449.64, -668.64) * mm, "radius": 3 * mm});
            skCircle(sketch, "E3.0.23.35", {"center": v(-271.84, -668.64) * mm, "radius": 3 * mm});
            skCircle(sketch, "E3.0.23.36", {"center": v(32.96, -668.64) * mm, "radius": 3 * mm});
            skCircle(sketch, "E3.0.23.37", {"center": v(-500.44, -668.64) * mm, "radius": 3 * mm});
            skCircle(sketch, "E3.0.23.38", {"center": v(-43.24, -668.64) * mm, "radius": 3 * mm});
            skCircle(sketch, "E3.0.23.39", {"center": v(-348.04, -668.64) * mm, "radius": 3 * mm});
            skCircle(sketch, "E3.0.23.40", {"center": v(-68.64, -668.64) * mm, "radius": 3 * mm});
            skCircle(sketch, "E3.0.23.41", {"center": v(-398.84, -668.64) * mm, "radius": 3 * mm});
            skCircle(sketch, "E3.0.23.42", {"center": v(-246.44, -668.64) * mm, "radius": 3 * mm});
            skCircle(sketch, "E3.0.23.44", {"center": v(32.96, -668.64) * mm, "radius": 3 * mm});
            skCircle(sketch, "E3.0.23.45", {"center": v(-195.64, -668.64) * mm, "radius": 3 * mm});
            skCircle(sketch, "E3.0.23.47", {"center": v(-322.64, -668.64) * mm, "radius": 3 * mm});
            skCircle(sketch, "E3.0.23.49", {"center": v(-17.84, -668.64) * mm, "radius": 3 * mm});
            skCircle(sketch, "E3.0.23.50", {"center": v(134.56, -668.64) * mm, "radius": 3 * mm});
            skCircle(sketch, "E3.0.23.51", {"center": v(-449.64, -668.64) * mm, "radius": 3 * mm});
            skCircle(sketch, "E3.0.23.53", {"center": v(-170.24, -668.64) * mm, "radius": 3 * mm});
            skCircle(sketch, "E3.0.23.54", {"center": v(-119.44, -668.64) * mm, "radius": 3 * mm});
            skCircle(sketch, "E3.0.23.55", {"center": v(-373.44, -668.64) * mm, "radius": 3 * mm});
            skCircle(sketch, "E3.0.23.56", {"center": v(109.16, -668.64) * mm, "radius": 3 * mm});
            skCircle(sketch, "E3.0.23.57", {"center": v(-424.24, -668.64) * mm, "radius": 3 * mm});
            skCircle(sketch, "E3.0.23.58", {"center": v(-525.84, -668.64) * mm, "radius": 3 * mm});
            skCircle(sketch, "E3.0.23.59", {"center": v(-94.04, -668.64) * mm, "radius": 3 * mm});
            skCircle(sketch, "E3.0.23.60", {"center": v(-475.04, -668.64) * mm, "radius": 3 * mm});
            skCircle(sketch, "E3.0.23.61", {"center": v(58.36, -668.64) * mm, "radius": 3 * mm});
            skCircle(sketch, "E3.0.23.63", {"center": v(7.56, -668.64) * mm, "radius": 3 * mm});
            skCircle(sketch, "E3.0.23.64", {"center": v(-297.24, -668.64) * mm, "radius": 3 * mm});
            skCircle(sketch, "E3.0.23.67", {"center": v(-144.84, -668.64) * mm, "radius": 3 * mm});
            skCircle(sketch, "E3.0.23.68", {"center": v(-221.04, -668.64) * mm, "radius": 3 * mm});
            skCircle(sketch, "E3.0.23.69", {"center": v(-271.84, -668.64) * mm, "radius": 3 * mm});
            skCircle(sketch, "E3.0.23.70", {"center": v(83.76, -668.64) * mm, "radius": 3 * mm});
            skCircle(sketch, "E3.0.23.71", {"center": v(134.56, -668.64) * mm, "radius": 3 * mm});
            skCircle(sketch, "E3.0.23.72", {"center": v(-424.24, -668.64) * mm, "radius": 3 * mm});
            skCircle(sketch, "E3.0.23.73", {"center": v(-195.64, -668.64) * mm, "radius": 3 * mm});
            skCircle(sketch, "E3.0.23.74", {"center": v(-525.84, -668.64) * mm, "radius": 3 * mm});
            skCircle(sketch, "E3.0.23.75", {"center": v(109.16, -668.64) * mm, "radius": 3 * mm});
            skCircle(sketch, "E3.0.23.76", {"center": v(-246.44, -668.64) * mm, "radius": 3 * mm});
            skCircle(sketch, "E3.0.23.77", {"center": v(-449.64, -668.64) * mm, "radius": 3 * mm});
            skCircle(sketch, "E3.0.23.78", {"center": v(-144.84, -668.64) * mm, "radius": 3 * mm});
            skCircle(sketch, "E3.0.23.79", {"center": v(-348.04, -668.64) * mm, "radius": 3 * mm});
            skCircle(sketch, "E3.0.23.80", {"center": v(-94.04, -668.64) * mm, "radius": 3 * mm});
            skCircle(sketch, "E3.0.23.81", {"center": v(32.96, -668.64) * mm, "radius": 3 * mm});
            skCircle(sketch, "E3.0.23.82", {"center": v(-68.64, -668.64) * mm, "radius": 3 * mm});
            skCircle(sketch, "E3.0.23.84", {"center": v(-373.44, -668.64) * mm, "radius": 3 * mm});
            skCircle(sketch, "E3.0.23.86", {"center": v(-170.24, -668.64) * mm, "radius": 3 * mm});
            skCircle(sketch, "E3.0.23.88", {"center": v(-17.84, -668.64) * mm, "radius": 3 * mm});
            skCircle(sketch, "E3.0.23.89", {"center": v(-221.04, -668.64) * mm, "radius": 3 * mm});
            skCircle(sketch, "E3.0.23.90", {"center": v(-119.44, -668.64) * mm, "radius": 3 * mm});
            skCircle(sketch, "E3.0.23.92", {"center": v(-475.04, -668.64) * mm, "radius": 3 * mm});
            skCircle(sketch, "E3.0.23.93", {"center": v(-297.24, -668.64) * mm, "radius": 3 * mm});
            skCircle(sketch, "E3.0.23.94", {"center": v(-43.24, -668.64) * mm, "radius": 3 * mm});
            skCircle(sketch, "E3.0.23.95", {"center": v(83.76, -668.64) * mm, "radius": 3 * mm});
            skCircle(sketch, "E3.0.23.97", {"center": v(-500.44, -668.64) * mm, "radius": 3 * mm});
            skCircle(sketch, "E3.0.23.98", {"center": v(-322.64, -668.64) * mm, "radius": 3 * mm});
            skCircle(sketch, "E3.0.23.100", {"center": v(-398.84, -668.64) * mm, "radius": 3 * mm});
            skCircle(sketch, "E3.0.23.102", {"center": v(58.36, -668.64) * mm, "radius": 3 * mm});
            skCircle(sketch, "E3.0.23.103", {"center": v(7.56, -668.64) * mm, "radius": 3 * mm});
            skCircle(sketch, "E3.0.23.104", {"center": v(-271.84, -668.64) * mm, "radius": 3 * mm});
            skLineSegment(sketch, "E4", {"start": v(-588.45, -721.98) * mm, "end": v(-588.45, -413.98) * mm});
            skSolve(sketch);
        }
        {
            var Q0;
            Q0=makeQuery(id+"F0.imprint","IMPRINT",FACE,{"disambiguationData":[TD([[makeQuery(id+"F0.imprint","IMPRINT",EDGE,{"derivedFrom":sQuery(id+"F0.wireOp",EDGE,"E0")}),1.0]])]});
            extrude(context, id + "F1", {"entities" : qUnion([Q0]), "depth" : 19.05 * mm, "offsetDistance" : 25.4 * mm});
        }
    });
